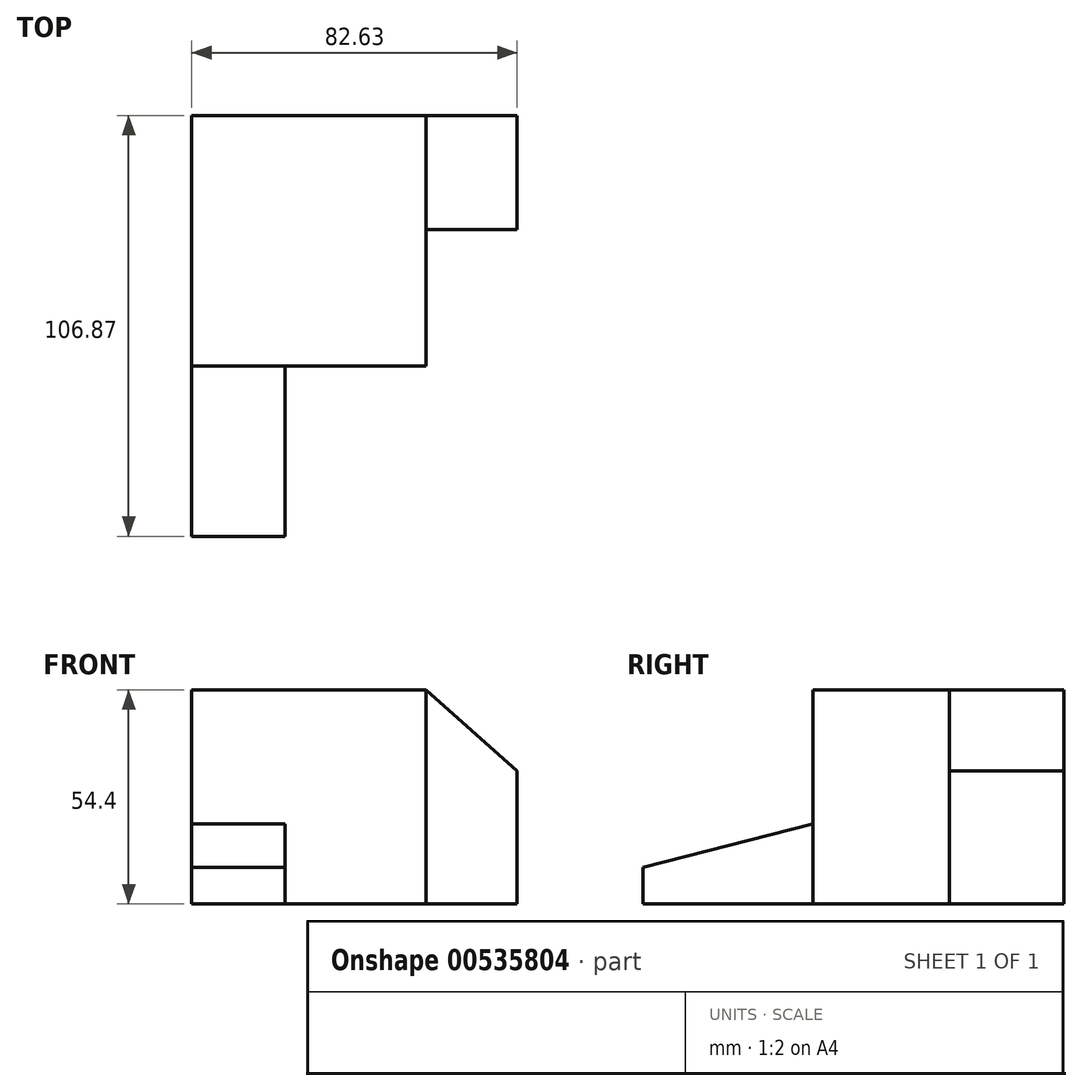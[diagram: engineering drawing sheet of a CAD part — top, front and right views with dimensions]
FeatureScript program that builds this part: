
annotation { "Feature Type Name" : "Feature", "Feature Type Description" : "" }
export const myFeature = defineFeature(function(context is Context, id is Id, definition is map)
    precondition{}
    {
        {
            var Q0;
            Q0=qCreatedBy(makeId("Top.planeOp"),FACE);
            var sketch = newSketch(context, id + "F0", { "sketchPlane" : qUnion([Q0])});
            skLineSegment(sketch, "E0.bottom", {"start": v(29.76, 31.82) * mm, "end": v(-29.76, 31.82) * mm});
            skLineSegment(sketch, "E0.top", {"start": v(29.76, -31.82) * mm, "end": v(-29.76, -31.82) * mm});
            skLineSegment(sketch, "E0.left", {"start": v(29.76, 31.82) * mm, "end": v(29.76, -31.82) * mm});
            skLineSegment(sketch, "E0.right", {"start": v(-29.76, 31.82) * mm, "end": v(-29.76, -31.82) * mm});
            skPoint(sketch, "E0.middle", {"position": v(0, 0) * mm});
            skSolve(sketch);
        }
        {
            var Q0;
            Q0=makeQuery(id+"F0.imprint","IMPRINT",FACE,{"disambiguationData":[TD([[makeQuery(id+"F0.imprint","IMPRINT",EDGE,{"derivedFrom":sQuery(id+"F0.wireOp",EDGE,"E0.bottom")}),1.0]])]});
            extrude(context, id + "F1", {"entities" : qUnion([Q0]), "endBound" : BoundingType.SYMMETRIC, "depth" : 54.4 * mm, "offsetDistance" : 25 * mm});
        }
        {
            var Q0;
            Q0=makeQuery(id+"F1.opExtrude","SWEPT_FACE",FACE,{"disambiguationData":[OSD([sQuery(id+"F0.wireOp",EDGE,"E0.bottom")])]});
            var sketch = newSketch(context, id + "F2", { "sketchPlane" : qUnion([Q0])});
            skLineSegment(sketch, "E1", {"start": v(-29.76, 27.2) * mm, "end": v(-52.87, 6.52) * mm});
            skLineSegment(sketch, "E2", {"start": v(-52.87, 6.52) * mm, "end": v(-52.87, -27.2) * mm});
            skLineSegment(sketch, "E3", {"start": v(-52.87, -27.2) * mm, "end": v(-29.76, -27.2) * mm});
            skLineSegment(sketch, "E4", {"start": v(-29.76, -27.2) * mm, "end": v(-29.76, 27.2) * mm});
            skSolve(sketch);
        }
        {
            var Q0;
            Q0=makeQuery(id+"F2.imprint","IMPRINT",FACE,{"disambiguationData":[TD([[makeQuery(id+"F2.imprint","IMPRINT",EDGE,{"derivedFrom":sQuery(id+"F2.wireOp",EDGE,"E1")}),1.0]])]});
            extrude(context, id + "F3", {"entities" : qUnion([Q0]), "operationType" : NewBodyOperationType.ADD, "oppositeDirection" : true, "depth" : 29 * mm, "offsetDistance" : 25 * mm});
        }
        {
            var Q0;
            Q0=makeQuery(id+"F1.opExtrude","SWEPT_FACE",FACE,{"disambiguationData":[OSD([sQuery(id+"F0.wireOp",EDGE,"E0.right")])]});
            var sketch = newSketch(context, id + "F4", { "sketchPlane" : qUnion([Q0])});
            skLineSegment(sketch, "E5", {"start": v(31.82, -27.2) * mm, "end": v(31.82, -6.84) * mm});
            skLineSegment(sketch, "E6", {"start": v(31.82, -6.84) * mm, "end": v(75.05, -17.87) * mm});
            skLineSegment(sketch, "E7", {"start": v(75.05, -17.87) * mm, "end": v(75.05, -27.2) * mm});
            skLineSegment(sketch, "E8", {"start": v(75.05, -27.2) * mm, "end": v(31.82, -27.2) * mm});
            skSolve(sketch);
        }
        {
            var Q0;
            Q0=makeQuery(id+"F4.imprint","IMPRINT",FACE,{"disambiguationData":[TD([[makeQuery(id+"F4.imprint","IMPRINT",EDGE,{"derivedFrom":sQuery(id+"F4.wireOp",EDGE,"E5")}),1.0]])]});
            extrude(context, id + "F5", {"entities" : qUnion([Q0]), "operationType" : NewBodyOperationType.ADD, "oppositeDirection" : true, "depth" : 23.7 * mm, "offsetDistance" : 25 * mm});
        }
    });
